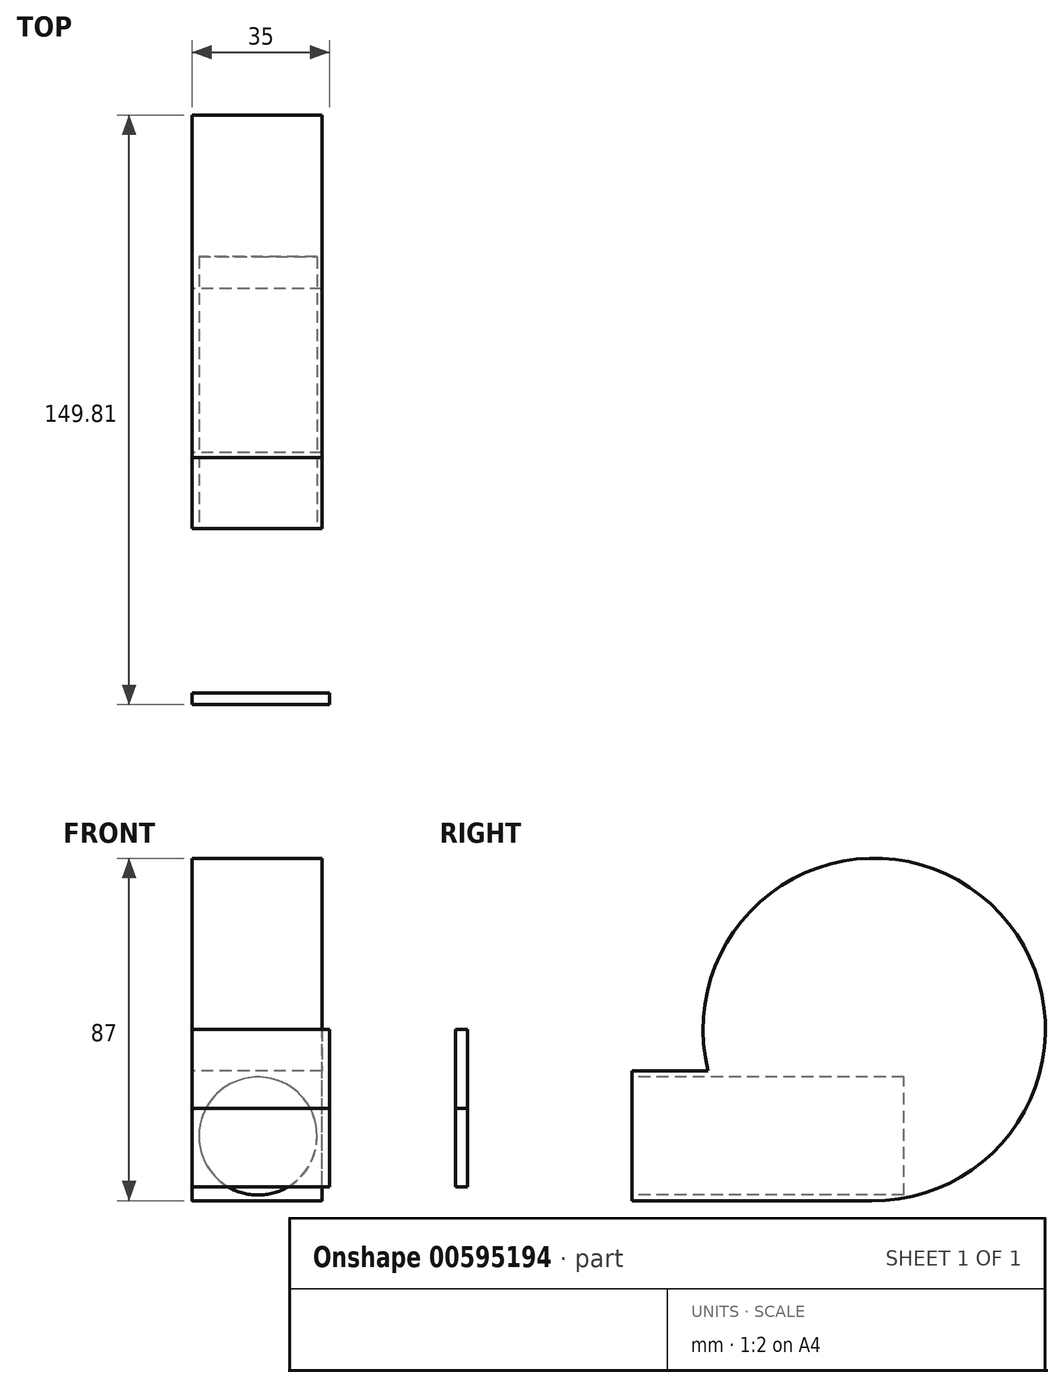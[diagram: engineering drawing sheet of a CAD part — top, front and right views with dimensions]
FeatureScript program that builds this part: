
annotation { "Feature Type Name" : "Feature", "Feature Type Description" : "" }
export const myFeature = defineFeature(function(context is Context, id is Id, definition is map)
    precondition{}
    {
        {
            var Q0;
            Q0=qCreatedBy(makeId("Right.planeOp"),FACE);
            var sketch = newSketch(context, id + "F0", { "sketchPlane" : qUnion([Q0])});
            skCircle(sketch, "E0", {"center": v(0, 0) * mm, "radius": 43.5 * mm});
            skLineSegment(sketch, "E1.bottom", {"start": v(-0.56, -43.5) * mm, "end": v(-61.56, -43.5) * mm});
            skLineSegment(sketch, "E1.top", {"start": v(-0.56, -10.5) * mm, "end": v(-61.56, -10.5) * mm});
            skLineSegment(sketch, "E1.left", {"start": v(-0.56, -43.5) * mm, "end": v(-0.56, -10.5) * mm});
            skLineSegment(sketch, "E1.right", {"start": v(-61.56, -43.5) * mm, "end": v(-61.56, -10.5) * mm});
            skSolve(sketch);
        }
        {
            var Q0;
            Q0 = qSketchRegion(id + "F0", true);
            extrude(context, id + "F1", {"entities" : qUnion([Q0]), "depth" : 33 * mm, "offsetDistance" : 25.4 * mm});
        }
        {
            var Q0;
            Q0=makeQuery(id+"F1.opExtrude","SWEPT_FACE",FACE,{"disambiguationData":[OSD([sQuery(id+"F0.wireOp",EDGE,"E1.right")])]});
            var sketch = newSketch(context, id + "F2", { "sketchPlane" : qUnion([Q0])});
            skCircle(sketch, "E2", {"center": v(16.76, -27.08) * mm, "radius": 15 * mm});
            skSolve(sketch);
        }
        {
            var Q0;
            Q0 = qSketchRegion(id + "F2", true);
            extrude(context, id + "F3", {"entities" : qUnion([Q0]), "operationType" : NewBodyOperationType.REMOVE, "oppositeDirection" : true, "depth" : 69.1 * mm, "offsetDistance" : 25.4 * mm});
        }
        {
            var Q0;
            Q0=qCreatedBy(makeId("Right.planeOp"),FACE);
            var sketch = newSketch(context, id + "F4", { "sketchPlane" : qUnion([Q0])});
            skLineSegment(sketch, "E3.bottom", {"start": v(-106.31, 0) * mm, "end": v(-103.31, 0) * mm});
            skLineSegment(sketch, "E3.top", {"start": v(-106.31, -20) * mm, "end": v(-103.31, -20) * mm});
            skLineSegment(sketch, "E3.left", {"start": v(-106.31, 0) * mm, "end": v(-106.31, -20) * mm});
            skLineSegment(sketch, "E3.right", {"start": v(-103.31, 0) * mm, "end": v(-103.31, -20) * mm});
            skSolve(sketch);
        }
        {
            var Q0;
            Q0=makeQuery(id+"F4.imprint","IMPRINT",FACE,{"disambiguationData":[TD([[makeQuery(id+"F4.imprint","IMPRINT",EDGE,{"derivedFrom":sQuery(id+"F4.wireOp",EDGE,"E3.bottom")}),-1.0]])]});
            extrude(context, id + "F5", {"entities" : qUnion([Q0]), "depth" : 35 * mm, "offsetDistance" : 25.4 * mm});
        }
        {
            var Q0;
            Q0=makeQuery(id+"F5.opExtrude","SWEPT_BODY",BODY,{"disambiguationData":[OSD([sQuery(id+"F4.wireOp",EDGE,"E3.bottom"),sQuery(id+"F4.wireOp",EDGE,"E3.top"),sQuery(id+"F4.wireOp",EDGE,"E3.left"),sQuery(id+"F4.wireOp",EDGE,"E3.right")])]});
            var Q1;
            Q1=makeQuery(id+"F5.opExtrude","SWEPT_FACE",FACE,{"disambiguationData":[OSD([sQuery(id+"F4.wireOp",EDGE,"E3.top")])]});
            mirror(context, id + "F6", {"operationType" : NewBodyOperationType.ADD, "entities" : qUnion([Q0]), "mirrorPlane" : qUnion([Q1])});
        }
    });
